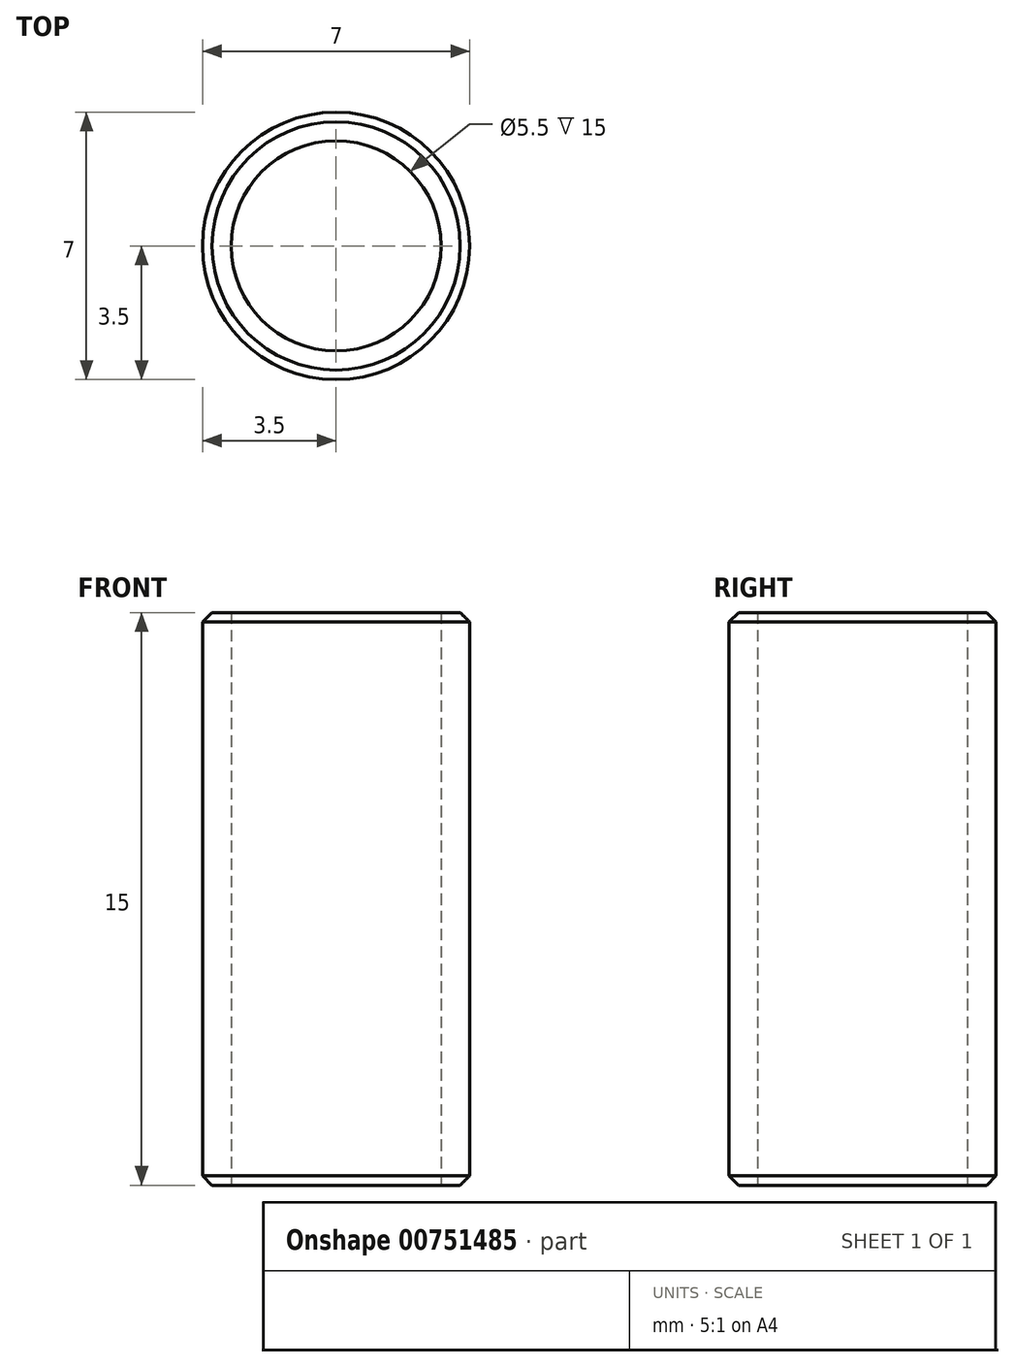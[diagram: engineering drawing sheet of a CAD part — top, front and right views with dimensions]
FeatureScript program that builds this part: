
annotation { "Feature Type Name" : "Feature", "Feature Type Description" : "" }
export const myFeature = defineFeature(function(context is Context, id is Id, definition is map)
    precondition{}
    {
        {
            assignVariable(context, id + "F0", {"name" : "SpacerHeight", "anyValue" : 15});
        }
        {
            var Q0;
            Q0=qCreatedBy(makeId("Top.planeOp"),FACE);
            var sketch = newSketch(context, id + "F1", { "sketchPlane" : qUnion([Q0])});
            skCircle(sketch, "E0", {"center": v(0, 0) * mm, "radius": 2.75 * mm});
            skCircle(sketch, "E1", {"center": v(0, 0) * mm, "radius": 3.5 * mm});
            skSolve(sketch);
        }
        {
            var Q0;
            Q0=makeQuery(id+"F1.imprint","IMPRINT",FACE,{"disambiguationData":[TD([[makeQuery(id+"F1.imprint","IMPRINT",EDGE,{"derivedFrom":sQuery(id+"F1.wireOp",EDGE,"E0")}),-1.0]])]});
            extrude(context, id + "F2", {"entities" : qUnion([Q0]), "depth" : (getVariable(context, 'SpacerHeight')) * mm, "offsetDistance" : 25 * mm});
        }
        {
            var Q0;
            Q0=makeQuery(id+"F2.opExtrude","CAP_EDGE",EDGE,{"disambiguationData":[OSD([sQuery(id+"F1.wireOp",EDGE,"E1")])],"isStart":false});
            var Q1;
            Q1=makeQuery(id+"F2.opExtrude","CAP_EDGE",EDGE,{"disambiguationData":[OSD([sQuery(id+"F1.wireOp",EDGE,"E1")])],"isStart":true});
            chamfer(context, id + "F3", {"entities" : qUnion([Q0, Q1]), "width" : .25 * mm, "tangentPropagation" : true});
        }
    });
